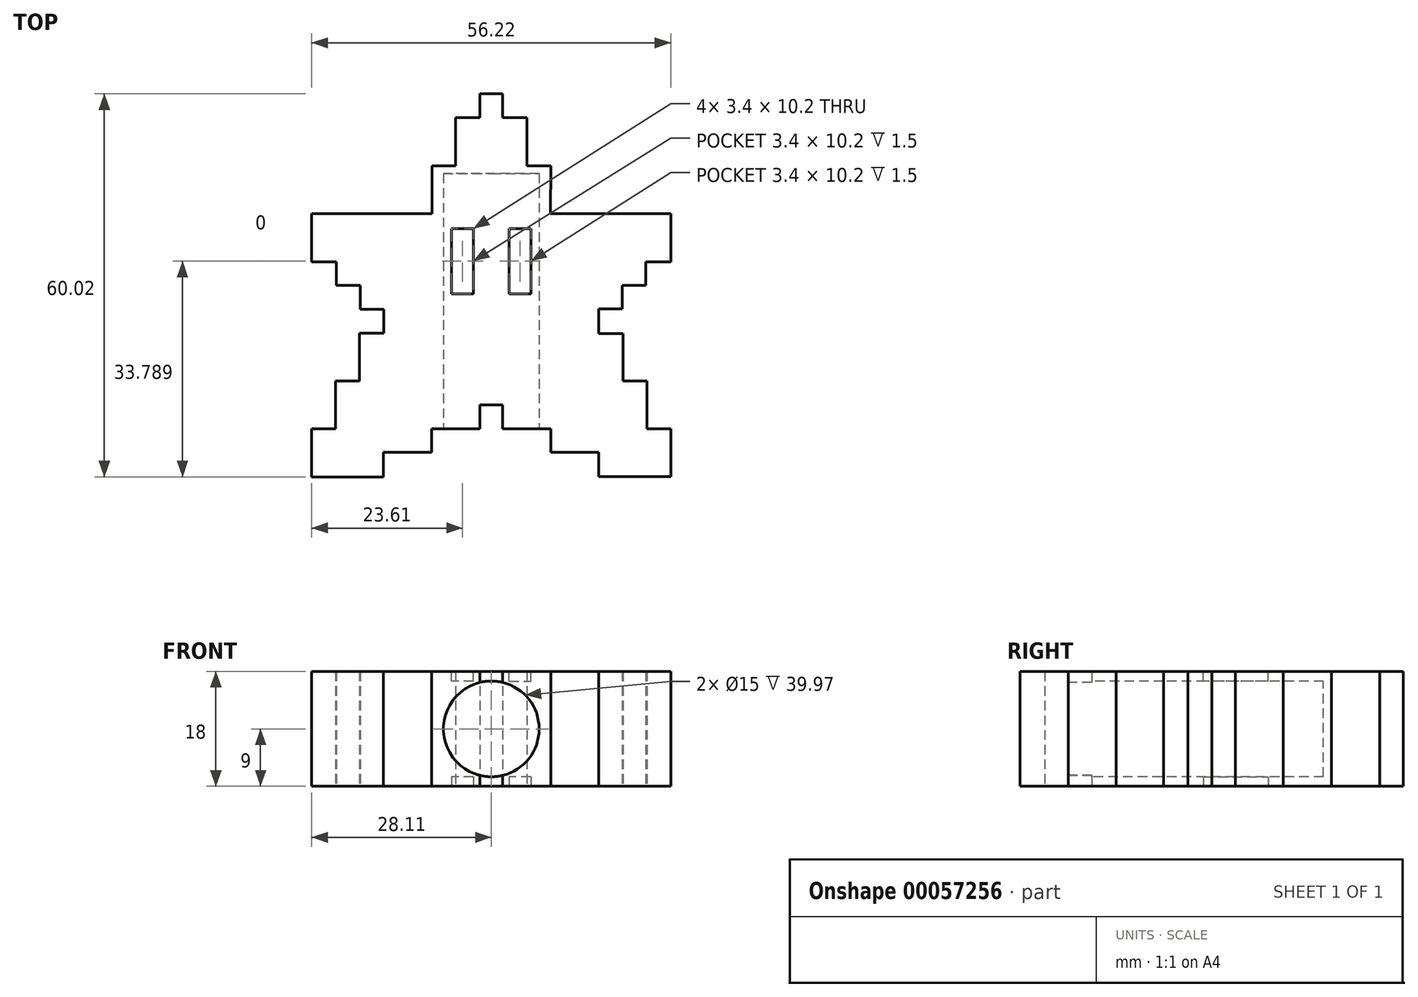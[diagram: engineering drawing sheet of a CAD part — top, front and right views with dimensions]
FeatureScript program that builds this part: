
annotation { "Feature Type Name" : "Feature", "Feature Type Description" : "" }
export const myFeature = defineFeature(function(context is Context, id is Id, definition is map)
    precondition{}
    {
        {
            var Q0;
            Q0=qCreatedBy(makeId("Top.planeOp"),FACE);
            var sketch = newSketch(context, id + "F0", { "sketchPlane" : qUnion([Q0])});
            skLineSegment(sketch, "E0", {"start": v(-1.77, 30) * mm, "end": v(1.75, 30) * mm});
            skLineSegment(sketch, "E1", {"start": v(1.75, 30) * mm, "end": v(1.75, 26.3) * mm});
            skLineSegment(sketch, "E2", {"start": v(1.75, 26.3) * mm, "end": v(5.59, 26.3) * mm});
            skLineSegment(sketch, "E3", {"start": v(5.59, 26.3) * mm, "end": v(5.59, 18.75) * mm});
            skLineSegment(sketch, "E4", {"start": v(5.59, 18.75) * mm, "end": v(9.35, 18.75) * mm});
            skLineSegment(sketch, "E5", {"start": v(9.35, 18.75) * mm, "end": v(9.28, 11.22) * mm});
            skLineSegment(sketch, "E6", {"start": v(9.28, 11.22) * mm, "end": v(28.11, 11.22) * mm});
            skLineSegment(sketch, "E7", {"start": v(28.11, 11.22) * mm, "end": v(28.11, 3.7) * mm});
            skLineSegment(sketch, "E8", {"start": v(28.11, 3.7) * mm, "end": v(24.21, 3.7) * mm});
            skLineSegment(sketch, "E9", {"start": v(24.21, 3.7) * mm, "end": v(24.21, 0.01) * mm});
            skLineSegment(sketch, "E10", {"start": v(24.21, 0.01) * mm, "end": v(20.52, 0.01) * mm});
            skLineSegment(sketch, "E11", {"start": v(20.52, 0.01) * mm, "end": v(20.52, -3.68) * mm});
            skLineSegment(sketch, "E12", {"start": v(20.52, -3.68) * mm, "end": v(16.83, -3.68) * mm});
            skLineSegment(sketch, "E13", {"start": v(16.83, -3.68) * mm, "end": v(16.83, -7.54) * mm});
            skLineSegment(sketch, "E14", {"start": v(16.83, -7.54) * mm, "end": v(20.64, -7.54) * mm});
            skLineSegment(sketch, "E15", {"start": v(20.64, -7.54) * mm, "end": v(20.64, -14.96) * mm});
            skLineSegment(sketch, "E16", {"start": v(20.64, -14.96) * mm, "end": v(24.36, -14.96) * mm});
            skLineSegment(sketch, "E17", {"start": v(24.36, -14.96) * mm, "end": v(24.36, -22.47) * mm});
            skLineSegment(sketch, "E18", {"start": v(24.36, -22.47) * mm, "end": v(28.1, -22.47) * mm});
            skLineSegment(sketch, "E19", {"start": v(28.1, -22.47) * mm, "end": v(28.1, -30) * mm});
            skLineSegment(sketch, "E20", {"start": v(28.1, -30) * mm, "end": v(16.85, -30) * mm});
            skLineSegment(sketch, "E21", {"start": v(16.85, -30) * mm, "end": v(16.85, -26.14) * mm});
            skLineSegment(sketch, "E22", {"start": v(16.85, -26.14) * mm, "end": v(9.3, -26.14) * mm});
            skLineSegment(sketch, "E23", {"start": v(9.3, -26.14) * mm, "end": v(9.3, -22.45) * mm});
            skLineSegment(sketch, "E24", {"start": v(9.3, -22.45) * mm, "end": v(1.77, -22.45) * mm});
            skLineSegment(sketch, "E25", {"start": v(1.77, -22.45) * mm, "end": v(1.77, -18.76) * mm});
            skLineSegment(sketch, "E26", {"start": v(1.77, -18.76) * mm, "end": v(-1.8, -18.76) * mm});
            skLineSegment(sketch, "E27", {"start": v(-1.8, -18.76) * mm, "end": v(-1.8, -22.45) * mm});
            skLineSegment(sketch, "E28", {"start": v(-1.8, -22.45) * mm, "end": v(-9.33, -22.45) * mm});
            skLineSegment(sketch, "E29", {"start": v(-9.33, -22.45) * mm, "end": v(-9.33, -26.14) * mm});
            skLineSegment(sketch, "E30", {"start": v(-9.33, -26.14) * mm, "end": v(-16.87, -26.14) * mm});
            skLineSegment(sketch, "E31", {"start": v(-16.87, -26.14) * mm, "end": v(-16.87, -30) * mm});
            skLineSegment(sketch, "E32", {"start": v(-16.87, -30) * mm, "end": v(-28.11, -30) * mm});
            skLineSegment(sketch, "E33", {"start": v(-28.11, -30) * mm, "end": v(-28.11, -22.46) * mm});
            skLineSegment(sketch, "E34", {"start": v(-28.11, -22.46) * mm, "end": v(-24.39, -22.46) * mm});
            skLineSegment(sketch, "E35", {"start": v(-24.39, -22.46) * mm, "end": v(-24.39, -15) * mm});
            skLineSegment(sketch, "E36", {"start": v(-24.39, -15) * mm, "end": v(-20.66, -15) * mm});
            skLineSegment(sketch, "E37", {"start": v(-20.66, -15) * mm, "end": v(-20.66, -7.52) * mm});
            skLineSegment(sketch, "E38", {"start": v(-20.66, -7.52) * mm, "end": v(-16.85, -7.52) * mm});
            skLineSegment(sketch, "E39", {"start": v(-16.85, -7.52) * mm, "end": v(-16.85, -3.76) * mm});
            skLineSegment(sketch, "E40", {"start": v(-16.85, -3.76) * mm, "end": v(-20.54, -3.76) * mm});
            skLineSegment(sketch, "E41", {"start": v(-20.54, -3.76) * mm, "end": v(-20.54, 0.01) * mm});
            skLineSegment(sketch, "E42", {"start": v(-20.54, 0.01) * mm, "end": v(-24.24, 0.01) * mm});
            skLineSegment(sketch, "E43", {"start": v(-24.24, 0.01) * mm, "end": v(-24.24, 3.7) * mm});
            skLineSegment(sketch, "E44", {"start": v(-24.24, 3.7) * mm, "end": v(-28.1, 3.7) * mm});
            skLineSegment(sketch, "E45", {"start": v(-28.1, 3.7) * mm, "end": v(-28.1, 11.22) * mm});
            skLineSegment(sketch, "E46", {"start": v(-28.1, 11.22) * mm, "end": v(-9.3, 11.22) * mm});
            skLineSegment(sketch, "E47", {"start": v(-9.3, 11.22) * mm, "end": v(-9.3, 18.75) * mm});
            skLineSegment(sketch, "E48", {"start": v(-9.3, 18.75) * mm, "end": v(-5.61, 18.75) * mm});
            skLineSegment(sketch, "E49", {"start": v(-5.61, 18.75) * mm, "end": v(-5.61, 26.3) * mm});
            skLineSegment(sketch, "E50", {"start": v(-5.61, 26.3) * mm, "end": v(-1.77, 26.3) * mm});
            skLineSegment(sketch, "E51", {"start": v(-1.77, 26.3) * mm, "end": v(-1.77, 30) * mm});
            skSolve(sketch);
        }
        {
            var Q0;
            Q0 = qSketchRegion(id + "F0", true);
            extrude(context, id + "F1", {"entities" : qUnion([Q0]), "depth" : 18 * mm});
        }
        {
            var Q0;
            Q0=makeQuery(id+"F1.opExtrude","SWEPT_FACE",FACE,{"disambiguationData":[OSD([sQuery(id+"F0.wireOp",EDGE,"E24")])]});
            var sketch = newSketch(context, id + "F2", { "sketchPlane" : qUnion([Q0])});
            skCircle(sketch, "E52", {"center": v(0, 9) * mm, "radius": 7.5 * mm});
            skPoint(sketch, "E52.centerSnap0", {"position": v(1.77, 9) * mm});
            skSolve(sketch);
        }
        {
            var Q0;
            Q0 = qSketchRegion(id + "F2", true);
            extrude(context, id + "F3", {"entities" : qUnion([Q0]), "operationType" : NewBodyOperationType.REMOVE, "oppositeDirection" : true, "depth" : 39.97 * mm});
        }
        {
            var Q0;
            Q0=makeQuery(id+"F1.opExtrude","CAP_FACE",FACE,{"disambiguationData":[OSD([sQuery(id+"F0.wireOp",EDGE,"E0"),sQuery(id+"F0.wireOp",EDGE,"E1"),sQuery(id+"F0.wireOp",EDGE,"E2"),sQuery(id+"F0.wireOp",EDGE,"E3"),sQuery(id+"F0.wireOp",EDGE,"E4"),sQuery(id+"F0.wireOp",EDGE,"E5"),sQuery(id+"F0.wireOp",EDGE,"E6"),sQuery(id+"F0.wireOp",EDGE,"E7"),sQuery(id+"F0.wireOp",EDGE,"E8"),sQuery(id+"F0.wireOp",EDGE,"E9"),sQuery(id+"F0.wireOp",EDGE,"E10"),sQuery(id+"F0.wireOp",EDGE,"E11"),sQuery(id+"F0.wireOp",EDGE,"E12"),sQuery(id+"F0.wireOp",EDGE,"E13"),sQuery(id+"F0.wireOp",EDGE,"E14"),sQuery(id+"F0.wireOp",EDGE,"E15"),sQuery(id+"F0.wireOp",EDGE,"E16"),sQuery(id+"F0.wireOp",EDGE,"E17"),sQuery(id+"F0.wireOp",EDGE,"E18"),sQuery(id+"F0.wireOp",EDGE,"E19"),sQuery(id+"F0.wireOp",EDGE,"E20"),sQuery(id+"F0.wireOp",EDGE,"E21"),sQuery(id+"F0.wireOp",EDGE,"E22"),sQuery(id+"F0.wireOp",EDGE,"E23"),sQuery(id+"F0.wireOp",EDGE,"E24"),sQuery(id+"F0.wireOp",EDGE,"E25"),sQuery(id+"F0.wireOp",EDGE,"E26"),sQuery(id+"F0.wireOp",EDGE,"E27"),sQuery(id+"F0.wireOp",EDGE,"E28"),sQuery(id+"F0.wireOp",EDGE,"E29"),sQuery(id+"F0.wireOp",EDGE,"E30"),sQuery(id+"F0.wireOp",EDGE,"E31"),sQuery(id+"F0.wireOp",EDGE,"E32"),sQuery(id+"F0.wireOp",EDGE,"E33"),sQuery(id+"F0.wireOp",EDGE,"E34"),sQuery(id+"F0.wireOp",EDGE,"E35"),sQuery(id+"F0.wireOp",EDGE,"E36"),sQuery(id+"F0.wireOp",EDGE,"E37"),sQuery(id+"F0.wireOp",EDGE,"E38"),sQuery(id+"F0.wireOp",EDGE,"E39"),sQuery(id+"F0.wireOp",EDGE,"E40"),sQuery(id+"F0.wireOp",EDGE,"E41"),sQuery(id+"F0.wireOp",EDGE,"E42"),sQuery(id+"F0.wireOp",EDGE,"E43"),sQuery(id+"F0.wireOp",EDGE,"E44"),sQuery(id+"F0.wireOp",EDGE,"E45"),sQuery(id+"F0.wireOp",EDGE,"E46"),sQuery(id+"F0.wireOp",EDGE,"E47"),sQuery(id+"F0.wireOp",EDGE,"E48"),sQuery(id+"F0.wireOp",EDGE,"E49"),sQuery(id+"F0.wireOp",EDGE,"E50"),sQuery(id+"F0.wireOp",EDGE,"E51")])],"isStart":false});
            var sketch = newSketch(context, id + "F4", { "sketchPlane" : qUnion([Q0])});
            skLineSegment(sketch, "E53.bottom", {"start": v(2.8, 8.88) * mm, "end": v(6.2, 8.88) * mm});
            skLineSegment(sketch, "E53.top", {"start": v(2.8, -1.32) * mm, "end": v(6.2, -1.32) * mm});
            skLineSegment(sketch, "E53.left", {"start": v(2.8, 8.88) * mm, "end": v(2.8, -1.32) * mm});
            skLineSegment(sketch, "E53.right", {"start": v(6.2, 8.88) * mm, "end": v(6.2, -1.32) * mm});
            skLineSegment(sketch, "E54.MirrorCS", {"start": v(-6.2, 8.88) * mm, "end": v(-6.2, -1.32) * mm});
            skLineSegment(sketch, "E55.MirrorCS", {"start": v(-2.8, 8.88) * mm, "end": v(-2.8, -1.32) * mm});
            skLineSegment(sketch, "E56.MirrorCS", {"start": v(-2.8, -1.32) * mm, "end": v(-6.2, -1.32) * mm});
            skLineSegment(sketch, "E57.MirrorCS", {"start": v(-2.8, 8.88) * mm, "end": v(-6.2, 8.88) * mm});
            skSolve(sketch);
        }
        {
            var Q0;
            Q0 = qSketchRegion(id + "F4", true);
            extrude(context, id + "F5", {"entities" : qUnion([Q0]), "operationType" : NewBodyOperationType.REMOVE, "oppositeDirection" : true, "depth" : 1.5 * mm});
        }
        {
            var Q0;
            Q0=makeQuery(id+"F1.opExtrude","CAP_FACE",FACE,{"disambiguationData":[OSD([sQuery(id+"F0.wireOp",EDGE,"E0"),sQuery(id+"F0.wireOp",EDGE,"E1"),sQuery(id+"F0.wireOp",EDGE,"E2"),sQuery(id+"F0.wireOp",EDGE,"E3"),sQuery(id+"F0.wireOp",EDGE,"E4"),sQuery(id+"F0.wireOp",EDGE,"E5"),sQuery(id+"F0.wireOp",EDGE,"E6"),sQuery(id+"F0.wireOp",EDGE,"E7"),sQuery(id+"F0.wireOp",EDGE,"E8"),sQuery(id+"F0.wireOp",EDGE,"E9"),sQuery(id+"F0.wireOp",EDGE,"E10"),sQuery(id+"F0.wireOp",EDGE,"E11"),sQuery(id+"F0.wireOp",EDGE,"E12"),sQuery(id+"F0.wireOp",EDGE,"E13"),sQuery(id+"F0.wireOp",EDGE,"E14"),sQuery(id+"F0.wireOp",EDGE,"E15"),sQuery(id+"F0.wireOp",EDGE,"E16"),sQuery(id+"F0.wireOp",EDGE,"E17"),sQuery(id+"F0.wireOp",EDGE,"E18"),sQuery(id+"F0.wireOp",EDGE,"E19"),sQuery(id+"F0.wireOp",EDGE,"E20"),sQuery(id+"F0.wireOp",EDGE,"E21"),sQuery(id+"F0.wireOp",EDGE,"E22"),sQuery(id+"F0.wireOp",EDGE,"E23"),sQuery(id+"F0.wireOp",EDGE,"E24"),sQuery(id+"F0.wireOp",EDGE,"E25"),sQuery(id+"F0.wireOp",EDGE,"E26"),sQuery(id+"F0.wireOp",EDGE,"E27"),sQuery(id+"F0.wireOp",EDGE,"E28"),sQuery(id+"F0.wireOp",EDGE,"E29"),sQuery(id+"F0.wireOp",EDGE,"E30"),sQuery(id+"F0.wireOp",EDGE,"E31"),sQuery(id+"F0.wireOp",EDGE,"E32"),sQuery(id+"F0.wireOp",EDGE,"E33"),sQuery(id+"F0.wireOp",EDGE,"E34"),sQuery(id+"F0.wireOp",EDGE,"E35"),sQuery(id+"F0.wireOp",EDGE,"E36"),sQuery(id+"F0.wireOp",EDGE,"E37"),sQuery(id+"F0.wireOp",EDGE,"E38"),sQuery(id+"F0.wireOp",EDGE,"E39"),sQuery(id+"F0.wireOp",EDGE,"E40"),sQuery(id+"F0.wireOp",EDGE,"E41"),sQuery(id+"F0.wireOp",EDGE,"E42"),sQuery(id+"F0.wireOp",EDGE,"E43"),sQuery(id+"F0.wireOp",EDGE,"E44"),sQuery(id+"F0.wireOp",EDGE,"E45"),sQuery(id+"F0.wireOp",EDGE,"E46"),sQuery(id+"F0.wireOp",EDGE,"E47"),sQuery(id+"F0.wireOp",EDGE,"E48"),sQuery(id+"F0.wireOp",EDGE,"E49"),sQuery(id+"F0.wireOp",EDGE,"E50"),sQuery(id+"F0.wireOp",EDGE,"E51")])],"isStart":true});
            var sketch = newSketch(context, id + "F6", { "sketchPlane" : qUnion([Q0])});
            skLineSegment(sketch, "E58.0.0", {"start": v(-2.8, -8.88) * mm, "end": v(-6.2, -8.88) * mm});
            skLineSegment(sketch, "E58.0.1", {"start": v(-6.2, -8.88) * mm, "end": v(-6.2, 1.32) * mm});
            skLineSegment(sketch, "E58.0.2", {"start": v(-6.2, 1.32) * mm, "end": v(-2.8, 1.32) * mm});
            skLineSegment(sketch, "E58.0.3", {"start": v(-2.8, 1.32) * mm, "end": v(-2.8, -8.88) * mm});
            skLineSegment(sketch, "E58.1.0", {"start": v(6.2, -8.88) * mm, "end": v(2.8, -8.88) * mm});
            skLineSegment(sketch, "E58.1.1", {"start": v(2.8, -8.88) * mm, "end": v(2.8, 1.32) * mm});
            skLineSegment(sketch, "E58.1.2", {"start": v(2.8, 1.32) * mm, "end": v(6.2, 1.32) * mm});
            skLineSegment(sketch, "E58.1.3", {"start": v(6.2, 1.32) * mm, "end": v(6.2, -8.88) * mm});
            skSolve(sketch);
        }
        {
            var Q0;
            Q0 = qSketchRegion(id + "F6", true);
            extrude(context, id + "F7", {"entities" : qUnion([Q0]), "operationType" : NewBodyOperationType.REMOVE, "oppositeDirection" : true, "depth" : 1.5 * mm});
        }
    });
